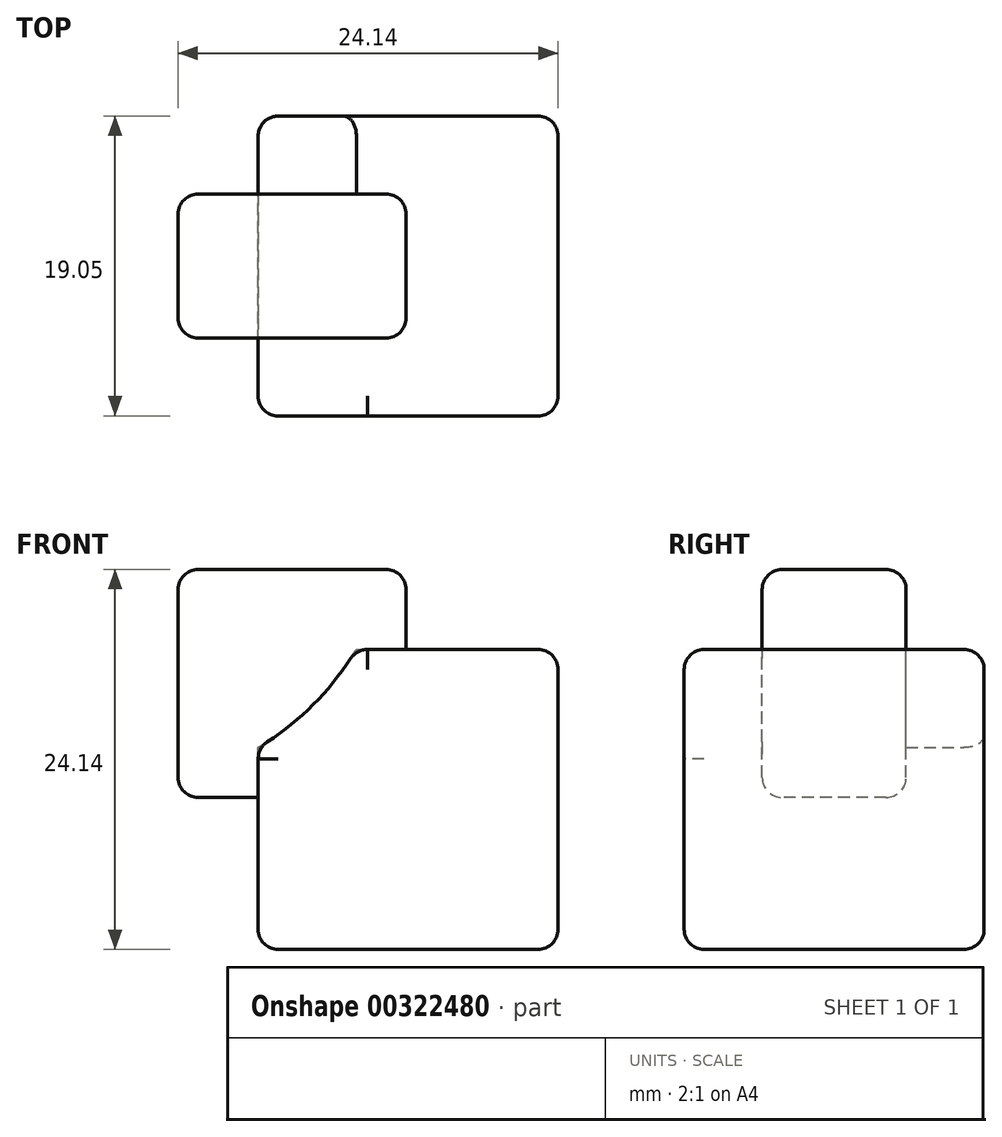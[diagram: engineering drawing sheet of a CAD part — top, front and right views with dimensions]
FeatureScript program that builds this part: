
annotation { "Feature Type Name" : "Feature", "Feature Type Description" : "" }
export const myFeature = defineFeature(function(context is Context, id is Id, definition is map)
    precondition{}
    {
        {
            var Q0;
            Q0=qCreatedBy(makeId("Front.planeOp"),FACE);
            var sketch = newSketch(context, id + "F0", { "sketchPlane" : qUnion([Q0])});
            skLineSegment(sketch, "E0.bottom", {"start": v(-9.52, -9.52) * mm, "end": v(9.53, -9.52) * mm});
            skLineSegment(sketch, "E0.top", {"start": v(-9.53, 9.53) * mm, "end": v(9.53, 9.53) * mm});
            skLineSegment(sketch, "E0.left", {"start": v(-9.52, -9.52) * mm, "end": v(-9.53, 9.53) * mm});
            skLineSegment(sketch, "E0.right", {"start": v(9.53, -9.52) * mm, "end": v(9.52, 9.53) * mm});
            skSolve(sketch);
        }
        {
            var Q0;
            Q0=makeQuery(id+"F0.imprint","IMPRINT",FACE,{"disambiguationData":[TD([[makeQuery(id+"F0.imprint","IMPRINT",EDGE,{"derivedFrom":sQuery(id+"F0.wireOp",EDGE,"E0.bottom")}),1.0]])]});
            extrude(context, id + "F1", {"entities" : qUnion([Q0]), "depth" : 19.05 * mm});
        }
        {
            var Q0;
            Q0=qCreatedBy(makeId("Front.planeOp"),FACE);
            cPlane(context, id + "F2", {"entities" : qUnion([Q0]), "cplaneType" : CPlaneType.OFFSET, "offset" : 9.52 * mm, "width" : 152.4 * mm, "height" : 152.4 * mm});
        }
        {
            var Q0;
            Q0=qCreatedBy(id+"F2.planeOp",FACE);
            var sketch = newSketch(context, id + "F3", { "sketchPlane" : qUnion([Q0])});
            skLineSegment(sketch, "E1.bottom", {"start": v(-0.13, 0.13) * mm, "end": v(-14.6, 0.13) * mm});
            skLineSegment(sketch, "E1.top", {"start": v(-0.13, 14.6) * mm, "end": v(-14.6, 14.6) * mm});
            skLineSegment(sketch, "E1.left", {"start": v(-0.13, 0.13) * mm, "end": v(-0.13, 14.6) * mm});
            skLineSegment(sketch, "E1.right", {"start": v(-14.6, 0.13) * mm, "end": v(-14.6, 14.6) * mm});
            skSolve(sketch);
        }
        {
            var Q0;
            Q0=makeQuery(id+"F1.opExtrude","CAP_FACE",FACE,{"disambiguationData":[OSD([sQuery(id+"F0.wireOp",EDGE,"E0.bottom"),sQuery(id+"F0.wireOp",EDGE,"E0.top"),sQuery(id+"F0.wireOp",EDGE,"E0.left"),sQuery(id+"F0.wireOp",EDGE,"E0.right")])],"isStart":true});
            var sketch = newSketch(context, id + "F4", { "sketchPlane" : qUnion([Q0])});
            skCircle(sketch, "E2", {"center": v(19.05, 19.05) * mm, "radius": 18.41 * mm});
            skLineSegment(sketch, "E3.bottom", {"start": v(9.53, 9.53) * mm, "end": v(1.9, 9.53) * mm});
            skLineSegment(sketch, "E3.top", {"start": v(9.53, 1.9) * mm, "end": v(1.9, 1.9) * mm});
            skLineSegment(sketch, "E3.left", {"start": v(9.53, 9.53) * mm, "end": v(9.53, 1.9) * mm});
            skLineSegment(sketch, "E3.right", {"start": v(1.9, 9.52) * mm, "end": v(1.9, 1.9) * mm});
            skSolve(sketch);
        }
        {
            var Q0;
            {var subQ4=sQuery(id+"F4.wireOp",EDGE,"E3.bottom");Q0=makeQuery(id+"F4.imprint","IMPRINT",FACE,{"disambiguationData":[TD([[makeQuery(id+"F4.imprint","IMPRINT",EDGE,{"derivedFrom":subQ4}),1.0]])]});}
            extrude(context, id + "F5", {"entities" : qUnion([Q0]), "operationType" : NewBodyOperationType.REMOVE, "endBound" : BoundingType.THROUGH_ALL, "oppositeDirection" : true, "depth" : 25.4 * mm});
        }
        {
            var Q0;
            Q0=makeQuery(id+"F3.imprint","IMPRINT",FACE,{"disambiguationData":[TD([[makeQuery(id+"F3.imprint","IMPRINT",EDGE,{"derivedFrom":sQuery(id+"F3.wireOp",EDGE,"E1.bottom")}),-1.0]])]});
            extrude(context, id + "F6", {"entities" : qUnion([Q0]), "operationType" : NewBodyOperationType.ADD, "endBound" : BoundingType.SYMMETRIC, "depth" : 9.14 * mm});
        }
        {
            var Q0;
            Q0=makeQuery(id+"F1.opExtrude","CAP_EDGE",EDGE,{"disambiguationData":[OSD([sQuery(id+"F0.wireOp",EDGE,"E0.top")])],"isStart":true});
            var Q1;
            Q1=makeQuery(id+"F1.opExtrude","CAP_EDGE",EDGE,{"disambiguationData":[OSD([sQuery(id+"F0.wireOp",EDGE,"E0.right")])],"isStart":false});
            var Q2;
            Q2=makeQuery(id+"F1.opExtrude","SWEPT_EDGE",EDGE,{"disambiguationData":[OSD([sQuery(id+"F0.wireOp",EDGE,"E0.bottom"),sQuery(id+"F0.wireOp",EDGE,"E0.right")])]});
            var Q3;
            Q3=makeQuery(id+"F1.opExtrude","SWEPT_EDGE",EDGE,{"disambiguationData":[OSD([sQuery(id+"F0.wireOp",EDGE,"E0.top"),sQuery(id+"F0.wireOp",EDGE,"E0.right")])]});
            var Q4;
            Q4=makeQuery(id+"F1.opExtrude","CAP_EDGE",EDGE,{"disambiguationData":[OSD([sQuery(id+"F0.wireOp",EDGE,"E0.right")])],"isStart":true});
            var Q5;
            Q5=makeQuery(id+"F1.opExtrude","CAP_EDGE",EDGE,{"disambiguationData":[OSD([sQuery(id+"F0.wireOp",EDGE,"E0.bottom")])],"isStart":false});
            var Q6;
            Q6=makeQuery(id+"F1.opExtrude","SWEPT_EDGE",EDGE,{"disambiguationData":[OSD([sQuery(id+"F0.wireOp",EDGE,"E0.bottom"),sQuery(id+"F0.wireOp",EDGE,"E0.left")])]});
            var Q7;
            Q7=makeQuery(id+"F1.opExtrude","CAP_EDGE",EDGE,{"disambiguationData":[OSD([sQuery(id+"F0.wireOp",EDGE,"E0.left")])],"isStart":false});
            var Q8;
            Q8=makeQuery(id+"F1.opExtrude","CAP_EDGE",EDGE,{"disambiguationData":[OSD([sQuery(id+"F0.wireOp",EDGE,"E0.top")])],"isStart":false});
            var Q9;
            Q9=makeQuery(id+"F1.opExtrude","CAP_EDGE",EDGE,{"disambiguationData":[OSD([sQuery(id+"F0.wireOp",EDGE,"E0.bottom")])],"isStart":true});
            var Q10;
            Q10=makeQuery(id+"F1.opExtrude","CAP_EDGE",EDGE,{"disambiguationData":[OSD([sQuery(id+"F0.wireOp",EDGE,"E0.left")])],"isStart":true});
            fillet(context, id + "F7", {"entities" : qUnion([Q0, Q1, Q2, Q3, Q4, Q5, Q6, Q7, Q8, Q9, Q10]), "radius" : 1.27 * mm, "tangentPropagation" : true, "allowEdgeOverflow" : false});
        }
        {
            var Q0;
            Q0=makeQuery(id+"F5.boolean.opBoolean","COPY",EDGE,{"derivedFrom":makeQuery(id+"F5.opExtrude","CAP_EDGE",EDGE,{"disambiguationData":[OSD([sQuery(id+"F4.wireOp",EDGE,"E2")])],"isStart":true})});
            var Q1;
            Q1=makeQuery(id+"F5.boolean.opBoolean","INTERSECT",EDGE,{"derivedFrom":[makeQuery(id+"F1.opExtrude","CAP_FACE",FACE,{"disambiguationData":[OSD([sQuery(id+"F0.wireOp",EDGE,"E0.bottom"),sQuery(id+"F0.wireOp",EDGE,"E0.top"),sQuery(id+"F0.wireOp",EDGE,"E0.left"),sQuery(id+"F0.wireOp",EDGE,"E0.right")])],"isStart":false}),makeQuery(id+"F5.opExtrude","SWEPT_FACE",FACE,{"disambiguationData":[OSD([sQuery(id+"F4.wireOp",EDGE,"E2")])]})]});
            fillet(context, id + "F8", {"entities" : qUnion([Q0, Q1]), "radius" : 1.27 * mm, "tangentPropagation" : true, "allowEdgeOverflow" : false});
        }
        {
            var Q0;
            Q0=makeQuery(id+"F6.opExtrude","CAP_EDGE",EDGE,{"disambiguationData":[OSD([sQuery(id+"F3.wireOp",EDGE,"E1.left")])],"isStart":true});
            var Q1;
            Q1=makeQuery(id+"F6.opExtrude","CAP_EDGE",EDGE,{"disambiguationData":[OSD([sQuery(id+"F3.wireOp",EDGE,"E1.top")])],"isStart":true});
            var Q2;
            Q2=makeQuery(id+"F6.opExtrude","SWEPT_EDGE",EDGE,{"disambiguationData":[OSD([sQuery(id+"F3.wireOp",EDGE,"E1.top"),sQuery(id+"F3.wireOp",EDGE,"E1.right")])]});
            var Q3;
            Q3=makeQuery(id+"F6.opExtrude","CAP_EDGE",EDGE,{"disambiguationData":[OSD([sQuery(id+"F3.wireOp",EDGE,"E1.right")])],"isStart":true});
            var Q4;
            Q4=makeQuery(id+"F6.opExtrude","CAP_EDGE",EDGE,{"disambiguationData":[OSD([sQuery(id+"F3.wireOp",EDGE,"E1.bottom")])],"isStart":true});
            var Q5;
            Q5=makeQuery(id+"F6.opExtrude","SWEPT_EDGE",EDGE,{"disambiguationData":[OSD([sQuery(id+"F3.wireOp",EDGE,"E1.bottom"),sQuery(id+"F3.wireOp",EDGE,"E1.right")])]});
            var Q6;
            Q6=makeQuery(id+"F6.opExtrude","CAP_EDGE",EDGE,{"disambiguationData":[OSD([sQuery(id+"F3.wireOp",EDGE,"E1.right")])],"isStart":false});
            var Q7;
            Q7=makeQuery(id+"F6.opExtrude","CAP_EDGE",EDGE,{"disambiguationData":[OSD([sQuery(id+"F3.wireOp",EDGE,"E1.top")])],"isStart":false});
            var Q8;
            Q8=makeQuery(id+"F6.opExtrude","CAP_EDGE",EDGE,{"disambiguationData":[OSD([sQuery(id+"F3.wireOp",EDGE,"E1.left")])],"isStart":false});
            var Q9;
            Q9=makeQuery(id+"F6.opExtrude","CAP_EDGE",EDGE,{"disambiguationData":[OSD([sQuery(id+"F3.wireOp",EDGE,"E1.bottom")])],"isStart":false});
            var Q10;
            Q10=makeQuery(id+"F6.opExtrude","SWEPT_EDGE",EDGE,{"disambiguationData":[OSD([sQuery(id+"F3.wireOp",EDGE,"E1.top"),sQuery(id+"F3.wireOp",EDGE,"E1.left")])]});
            fillet(context, id + "F9", {"entities" : qUnion([Q0, Q1, Q2, Q3, Q4, Q5, Q6, Q7, Q8, Q9, Q10]), "radius" : 1.27 * mm, "tangentPropagation" : true, "allowEdgeOverflow" : false});
        }
    });
